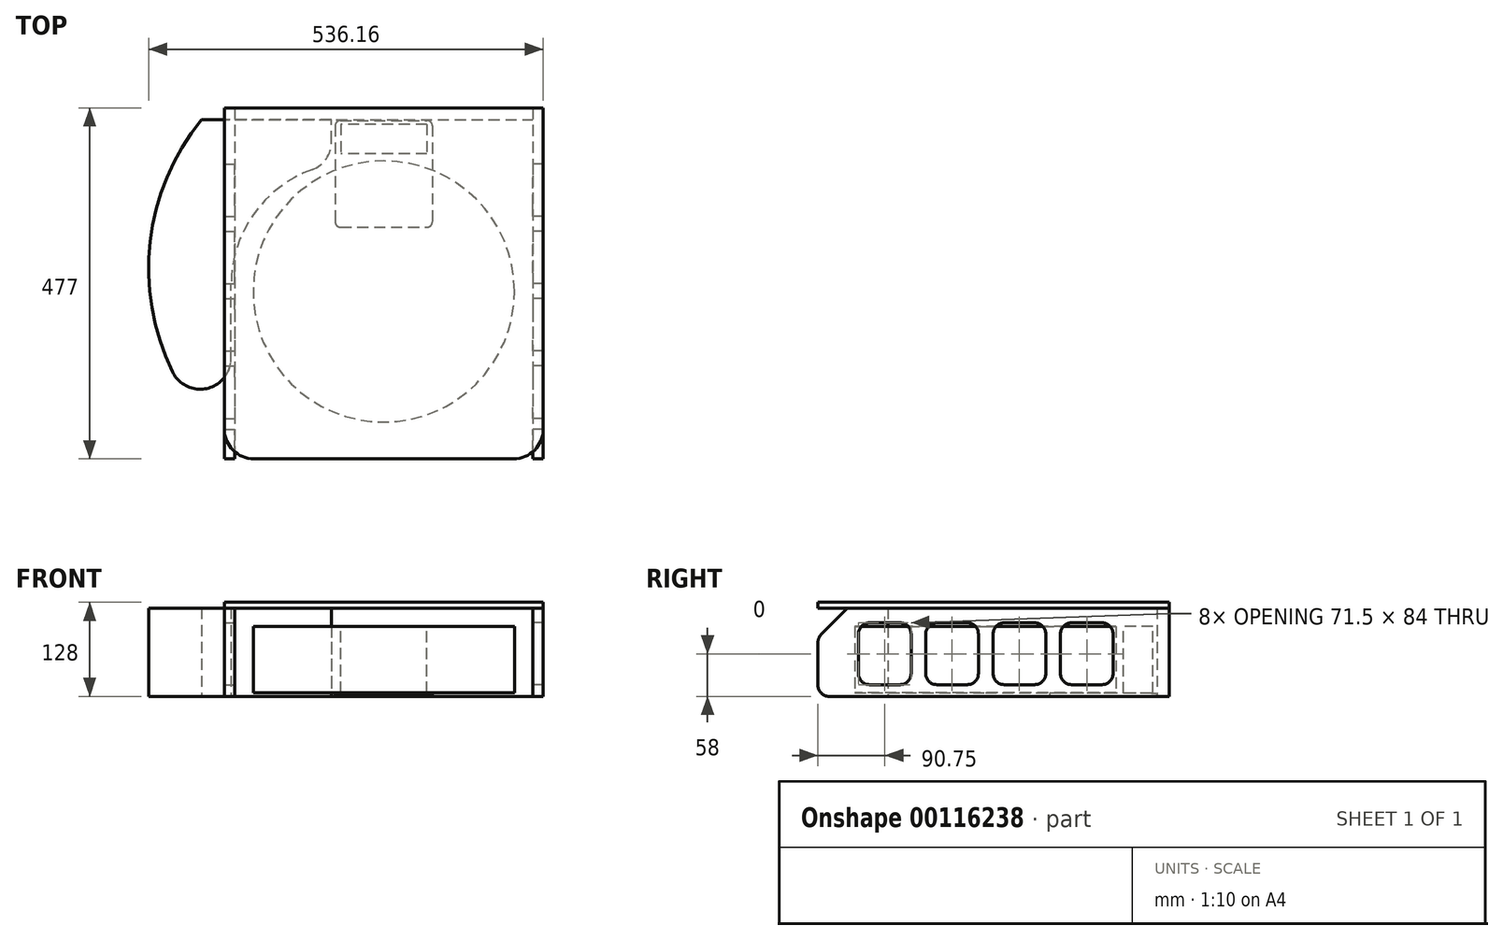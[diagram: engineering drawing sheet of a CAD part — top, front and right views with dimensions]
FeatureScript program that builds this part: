
annotation { "Feature Type Name" : "Feature", "Feature Type Description" : "" }
export const myFeature = defineFeature(function(context is Context, id is Id, definition is map)
    precondition{}
    {
        {
            var Q0;
            Q0=qCreatedBy(makeId("Front.planeOp"),FACE);
            var sketch = newSketch(context, id + "F0", { "sketchPlane" : qUnion([Q0])});
            skLineSegment(sketch, "E0", {"start": v(0, 0) * mm, "end": v(0, 117.94) * mm, "construction": true});
            skPoint(sketch, "E1", {"position": v(0, 5) * mm});
            skPoint(sketch, "E2", {"position": v(0, 95) * mm});
            skSolve(sketch);
        }
        {
            var Q0;
            Q0=qCreatedBy(makeId("Top.planeOp"),FACE);
            var Q1;
            Q1=sQuery(id+"F0.wireOp",VERTEX,"E1");
            cPlane(context, id + "F1", {"entities" : qUnion([Q0, Q1]), "cplaneType" : CPlaneType.PLANE_POINT, "offset" : 25 * mm, "width" : 150 * mm, "height" : 150 * mm});
        }
        {
            var Q0;
            Q0=qCreatedBy(id+"F1.planeOp",FACE);
            var sketch = newSketch(context, id + "F2", { "sketchPlane" : qUnion([Q0])});
            skCircle(sketch, "E3", {"center": v(0, 0) * mm, "radius": 177.5 * mm});
            skSolve(sketch);
        }
        {
            var Q0;
            Q0=qSketchRegion(id+"F2",true);
            extrude(context, id + "F3", {"entities" : qUnion([Q0]), "depth" : 90 * mm});
        }
        {
            var Q0;
            Q0=qCreatedBy(id+"F1.planeOp",FACE);
            var sketch = newSketch(context, id + "F4", { "sketchPlane" : qUnion([Q0])});
            skLineSegment(sketch, "E4.bottom", {"start": v(-58.5, 227.5) * mm, "end": v(58.5, 227.5) * mm});
            skLineSegment(sketch, "E4.top", {"start": v(-58.5, 187.5) * mm, "end": v(58.5, 187.5) * mm});
            skLineSegment(sketch, "E4.left", {"start": v(-58.5, 187.5) * mm, "end": v(-58.5, 227.5) * mm});
            skLineSegment(sketch, "E4.right", {"start": v(58.5, 187.5) * mm, "end": v(58.5, 227.5) * mm});
            skLineSegment(sketch, "E5", {"start": v(0, 0) * mm, "end": v(0, 187.5) * mm, "construction": true});
            skSolve(sketch);
        }
        {
            var Q0;
            Q0=qSketchRegion(id+"F4",true);
            var Q1;
            Q1=qCreatedBy(makeId("Top.planeOp"),FACE);
            var Q2;
            Q2=makeQuery(id+"F3.opExtrude","CAP_FACE",FACE,{"disambiguationData":[OSD([sQuery(id+"F2.wireOp",EDGE,"E3")])],"isStart":false});
            extrude(context, id + "F5", {"entities" : qUnion([Q0]), "endBound" : BoundingType.UP_TO_SURFACE, "oppositeDirection" : true, "endBoundEntityFace" : qUnion([Q1]), "depth" : 100 * mm, "hasSecondDirection" : true, "secondDirectionBound" : SecondDirectionBoundingType.UP_TO_SURFACE, "secondDirectionOppositeDirection" : false, "secondDirectionBoundEntityFace" : qUnion([Q2]), "secondDirectionDepth" : 25 * mm});
        }
        {
            var Q0;
            Q0=qCreatedBy(makeId("Top.planeOp"),FACE);
            var sketch = newSketch(context, id + "F6", { "sketchPlane" : qUnion([Q0])});
            skLineSegment(sketch, "E6.bottom", {"start": v(-59, 232.5) * mm, "end": v(59, 232.5) * mm});
            skLineSegment(sketch, "E6.top", {"start": v(-59, 87.5) * mm, "end": v(59, 87.5) * mm});
            skLineSegment(sketch, "E6.left", {"start": v(-66, 225.5) * mm, "end": v(-66, 94.5) * mm});
            skLineSegment(sketch, "E6.right", {"start": v(66, 225.5) * mm, "end": v(66, 94.5) * mm});
            skPoint(sketch, "E7.visualSharp", {"position": v(-66, 232.5) * mm});
            skArc(sketch, "E7.filletArc", {"start": v(-59, 232.5) * mm, "mid": v(-63.95, 230.45) * mm, "end": v(-66, 225.5) * mm});
            skPoint(sketch, "E8.visualSharp", {"position": v(66, 232.5) * mm});
            skArc(sketch, "E8.filletArc", {"start": v(66, 225.5) * mm, "mid": v(63.95, 230.45) * mm, "end": v(59, 232.5) * mm});
            skPoint(sketch, "E9.visualSharp", {"position": v(66, 87.5) * mm});
            skArc(sketch, "E9.filletArc", {"start": v(59, 87.5) * mm, "mid": v(63.95, 89.55) * mm, "end": v(66, 94.5) * mm});
            skPoint(sketch, "E10.visualSharp", {"position": v(-66, 87.5) * mm});
            skArc(sketch, "E10.filletArc", {"start": v(-66, 94.5) * mm, "mid": v(-63.95, 89.55) * mm, "end": v(-59, 87.5) * mm});
            skLineSegment(sketch, "E11", {"start": v(0, 0) * mm, "end": v(0, 87.5) * mm, "construction": true});
            skSolve(sketch);
        }
        {
            var Q0;
            Q0=qSketchRegion(id+"F6",true);
            extrude(context, id + "F7", {"entities" : qUnion([Q0]), "operationType" : NewBodyOperationType.ADD, "depth" : 4.5 * mm});
        }
        {
            var Q0;
            Q0=makeQuery(id+"F2.imprint","IMPRINT",FACE,{"disambiguationData":[TD([[makeQuery(id+"F2.imprint","IMPRINT",EDGE,{"derivedFrom":sQuery(id+"F2.wireOp",EDGE,"E3")}),1.0]])]});
            var sketch = newSketch(context, id + "F8", { "sketchPlane" : qUnion([Q0])});
            skLineSegment(sketch, "E12", {"start": v(0, -177.5) * mm, "end": v(0, 233.5) * mm, "construction": true});
            skLineSegment(sketch, "E13", {"start": v(-177.5, 233.5) * mm, "end": v(0, 233.5) * mm, "construction": true});
            skLineSegment(sketch, "E14", {"start": v(-177.5, 233.5) * mm, "end": v(-177.5, -177.5) * mm, "construction": true});
            skLineSegment(sketch, "E15", {"start": v(0, -177.5) * mm, "end": v(-177.5, -177.5) * mm, "construction": true});
            skSolve(sketch);
        }
        {
            var Q0;
            Q0=qCreatedBy(makeId("Front.planeOp"),FACE);
            var Q1;
            Q1=sQuery(id+"F8.wireOp",VERTEX,"E12.end");
            cPlane(context, id + "F9", {"entities" : qUnion([Q0, Q1]), "cplaneType" : CPlaneType.PLANE_POINT, "offset" : 25 * mm, "width" : 150 * mm, "height" : 150 * mm});
        }
        {
            var Q0;
            Q0=qCreatedBy(id+"F9.planeOp",FACE);
            var sketch = newSketch(context, id + "F10", { "sketchPlane" : qUnion([Q0])});
            skLineSegment(sketch, "E16.bottom", {"start": v(-202.5, 120) * mm, "end": v(0, 120) * mm});
            skLineSegment(sketch, "E16.top", {"start": v(-202.5, 0) * mm, "end": v(0, 0) * mm});
            skLineSegment(sketch, "E16.left", {"start": v(-202.5, 120) * mm, "end": v(-202.5, 0) * mm});
            skLineSegment(sketch, "E16.right", {"start": v(0, 120) * mm, "end": v(0, 0) * mm});
            skLineSegment(sketch, "E17", {"start": v(-156.5, 114) * mm, "end": v(-200.5, 114) * mm, "construction": true});
            skLineSegment(sketch, "E18", {"start": v(-200.5, 114) * mm, "end": v(-200.5, 76.5) * mm, "construction": true});
            skLineSegment(sketch, "E19", {"start": v(-156.5, 76.5) * mm, "end": v(-156.5, 114) * mm, "construction": true});
            skLineSegment(sketch, "E20", {"start": v(-156.5, 76.5) * mm, "end": v(-200.5, 76.5) * mm, "construction": true});
            skLineSegment(sketch, "E21", {"start": v(-156.5, 90) * mm, "end": v(-162.5, 90) * mm, "construction": true});
            skLineSegment(sketch, "E22", {"start": v(-162.5, 90) * mm, "end": v(-194.5, 90) * mm, "construction": true});
            skLineSegment(sketch, "E23", {"start": v(-194.5, 90) * mm, "end": v(-200.5, 90) * mm, "construction": true});
            skLineSegment(sketch, "E24", {"start": v(-156.5, 108) * mm, "end": v(-162.5, 108) * mm, "construction": true});
            skLineSegment(sketch, "E25", {"start": v(-162.5, 108) * mm, "end": v(-194.5, 108) * mm, "construction": true});
            skLineSegment(sketch, "E26", {"start": v(-194.5, 108) * mm, "end": v(-200.5, 108) * mm, "construction": true});
            skCircle(sketch, "E27", {"center": v(-162.5, 108) * mm, "radius": 2 * mm, "construction": true});
            skCircle(sketch, "E28", {"center": v(-194.5, 108) * mm, "radius": 2 * mm, "construction": true});
            skCircle(sketch, "E29", {"center": v(-194.5, 90) * mm, "radius": 2 * mm, "construction": true});
            skCircle(sketch, "E30", {"center": v(-162.5, 90) * mm, "radius": 2 * mm, "construction": true});
            skLineSegment(sketch, "E31", {"start": v(-162.5, 90) * mm, "end": v(-194.5, 108) * mm, "construction": true});
            skLineSegment(sketch, "E32", {"start": v(-162.5, 108) * mm, "end": v(-194.5, 90) * mm, "construction": true});
            skPoint(sketch, "E33", {"position": v(-178.5, 99) * mm});
            skSolve(sketch);
        }
        {
            var Q0;
            Q0=qSketchRegion(id+"F10",true);
            extrude(context, id + "F11", {"entities" : qUnion([Q0]), "oppositeDirection" : true, "depth" : 16 * mm});
        }
        {
            var Q0;
            Q0=makeQuery(id+"F11.opExtrude","SWEPT_FACE",FACE,{"disambiguationData":[OSD([sQuery(id+"F10.wireOp",EDGE,"E16.top")])]});
            var sketch = newSketch(context, id + "F12", { "sketchPlane" : qUnion([Q0])});
            skLineSegment(sketch, "E34", {"start": v(-247.44, -233.5) * mm, "end": v(-71, -233.5) * mm});
            skLineSegment(sketch, "E35", {"start": v(-71, -233.5) * mm, "end": v(-71, -203.5) * mm});
            skArc(sketch, "E36", {"start": v(-71, -203.5) * mm, "mid": v(-78.23, -180.56) * mm, "end": v(-97.32, -165.91) * mm});
            skArc(sketch, "E37", {"start": v(-207.5, -8.56) * mm, "mid": v(-177.22, -104.6) * mm, "end": v(-97.32, -165.91) * mm});
            skArc(sketch, "E38", {"start": v(-287.2, 109.22) * mm, "mid": v(-317.53, -67.96) * mm, "end": v(-247.44, -233.5) * mm});
            skLineSegment(sketch, "E39", {"start": v(-207.5, -8.56) * mm, "end": v(-207.5, 90.8) * mm});
            skArc(sketch, "E40", {"start": v(-207.5, 90.8) * mm, "mid": v(-240.02, 131.7) * mm, "end": v(-287.2, 109.22) * mm});
            skLineSegment(sketch, "E41", {"start": v(-71, -203.5) * mm, "end": v(-111, -203.5) * mm, "construction": true});
            skLineSegment(sketch, "E42", {"start": v(-111, -203.5) * mm, "end": v(-97.32, -165.91) * mm, "construction": true});
            skSolve(sketch);
        }
        {
            var Q0;
            Q0=qCreatedBy(makeId("Front.planeOp"),FACE);
            var Q1;
            Q1=sQuery(id+"F8.wireOp",VERTEX,"E15.start");
            cPlane(context, id + "F13", {"entities" : qUnion([Q0, Q1]), "cplaneType" : CPlaneType.PLANE_POINT, "offset" : 25 * mm, "width" : 150 * mm, "height" : 150 * mm});
        }
        {
            var Q0;
            Q0=makeQuery(id+"F11.opExtrude","SWEPT_FACE",FACE,{"disambiguationData":[OSD([sQuery(id+"F10.wireOp",EDGE,"E16.left")])]});
            var sketch = newSketch(context, id + "F14", { "sketchPlane" : qUnion([Q0])});
            skLineSegment(sketch, "E43", {"start": v(-249.5, 120) * mm, "end": v(-249.5, 0) * mm});
            skLineSegment(sketch, "E44", {"start": v(227.5, 0) * mm, "end": v(-249.5, 0) * mm});
            skLineSegment(sketch, "E45", {"start": v(227.5, 0) * mm, "end": v(227.5, 80) * mm});
            skLineSegment(sketch, "E46", {"start": v(227.5, 80) * mm, "end": v(187.5, 120) * mm});
            skLineSegment(sketch, "E47", {"start": v(-249.5, 120) * mm, "end": v(187.5, 120) * mm});
            skLineSegment(sketch, "E48.bottom", {"start": v(-102, 100) * mm, "end": v(-173.5, 100) * mm});
            skLineSegment(sketch, "E48.top", {"start": v(-102, 16) * mm, "end": v(-173.5, 16) * mm});
            skLineSegment(sketch, "E48.left", {"start": v(-173.5, 100) * mm, "end": v(-173.5, 16) * mm});
            skLineSegment(sketch, "E48.right", {"start": v(-102, 100) * mm, "end": v(-102, 16) * mm});
            skLineSegment(sketch, "E49.bottom", {"start": v(-10.5, 100) * mm, "end": v(-82, 100) * mm});
            skLineSegment(sketch, "E49.left", {"start": v(-82, 100) * mm, "end": v(-82, 16) * mm});
            skLineSegment(sketch, "E50.top", {"start": v(-10.5, 16) * mm, "end": v(-82, 16) * mm});
            skLineSegment(sketch, "E50.left", {"start": v(-10.5, 100) * mm, "end": v(-10.5, 16) * mm});
            skLineSegment(sketch, "E51.bottom", {"start": v(101, 100) * mm, "end": v(172.5, 100) * mm});
            skLineSegment(sketch, "E51.top", {"start": v(101, 16) * mm, "end": v(172.5, 16) * mm});
            skLineSegment(sketch, "E51.left", {"start": v(101, 100) * mm, "end": v(101, 16) * mm});
            skLineSegment(sketch, "E51.right", {"start": v(172.5, 100) * mm, "end": v(172.5, 16) * mm});
            skLineSegment(sketch, "E52", {"start": v(227.5, 80) * mm, "end": v(227.5, 120) * mm, "construction": true});
            skLineSegment(sketch, "E53.bottom", {"start": v(9.5, 100) * mm, "end": v(81, 100) * mm});
            skLineSegment(sketch, "E53.top", {"start": v(9.5, 16) * mm, "end": v(81, 16) * mm});
            skLineSegment(sketch, "E53.left", {"start": v(81, 100) * mm, "end": v(81, 16) * mm});
            skLineSegment(sketch, "E53.right", {"start": v(9.5, 100) * mm, "end": v(9.5, 16) * mm});
            skPoint(sketch, "E54", {"position": v(101, 120) * mm});
            skLineSegment(sketch, "E55", {"start": v(187.5, 120) * mm, "end": v(187.5, 0) * mm, "construction": true});
            skLineSegment(sketch, "E56", {"start": v(-102, 16) * mm, "end": v(-82, 16) * mm, "construction": true});
            skLineSegment(sketch, "E57", {"start": v(9.5, 16) * mm, "end": v(-10.5, 16) * mm, "construction": true});
            skLineSegment(sketch, "E58", {"start": v(81, 16) * mm, "end": v(101, 16) * mm, "construction": true});
            skPoint(sketch, "E59", {"position": v(177.5, 23.11) * mm});
            skSolve(sketch);
        }
        {
            var Q0;
            Q0=qSketchRegion(id+"F14",true);
            extrude(context, id + "F15", {"entities" : qUnion([Q0]), "depth" : 14 * mm});
        }
        {
            var Q0;
            Q0=makeQuery(id+"F15.opExtrude","SWEPT_FACE",FACE,{"disambiguationData":[OSD([sQuery(id+"F14.wireOp",EDGE,"E47")])]});
            var sketch = newSketch(context, id + "F16", { "sketchPlane" : qUnion([Q0])});
            skLineSegment(sketch, "E60", {"start": v(-216.5, -144.25) * mm, "end": v(-202.5, -144.25) * mm, "construction": true});
            skCircle(sketch, "E61", {"center": v(-209.5, -144.25) * mm, "radius": 5.05 * mm});
            skSolve(sketch);
        }
        {
            var Q0;
            Q0=makeQuery(id+"F15.opExtrude","SWEPT_EDGE",EDGE,{"disambiguationData":[OSD([sQuery(id+"F14.wireOp",EDGE,"E49.bottom"),sQuery(id+"F14.wireOp",EDGE,"E49.left")])]});
            var Q1;
            Q1=makeQuery(id+"F15.opExtrude","SWEPT_EDGE",EDGE,{"disambiguationData":[OSD([sQuery(id+"F14.wireOp",EDGE,"E48.bottom"),sQuery(id+"F14.wireOp",EDGE,"E48.left")])]});
            var Q2;
            Q2=makeQuery(id+"F15.opExtrude","SWEPT_EDGE",EDGE,{"disambiguationData":[OSD([sQuery(id+"F14.wireOp",EDGE,"E50.bottom"),sQuery(id+"F14.wireOp",EDGE,"E50.left")])]});
            var Q3;
            Q3=makeQuery(id+"F15.opExtrude","SWEPT_EDGE",EDGE,{"disambiguationData":[OSD([sQuery(id+"F14.wireOp",EDGE,"E44"),sQuery(id+"F14.wireOp",EDGE,"E45")])]});
            var Q4;
            Q4=makeQuery(id+"F15.opExtrude","SWEPT_EDGE",EDGE,{"disambiguationData":[OSD([sQuery(id+"F14.wireOp",EDGE,"E45"),sQuery(id+"F14.wireOp",EDGE,"E46")])]});
            var Q5;
            Q5=makeQuery(id+"F15.opExtrude","SWEPT_EDGE",EDGE,{"disambiguationData":[OSD([sQuery(id+"F14.wireOp",EDGE,"E48.top"),sQuery(id+"F14.wireOp",EDGE,"E48.left")])]});
            var Q6;
            Q6=makeQuery(id+"F15.opExtrude","SWEPT_EDGE",EDGE,{"disambiguationData":[OSD([sQuery(id+"F14.wireOp",EDGE,"E49.top"),sQuery(id+"F14.wireOp",EDGE,"E49.left")])]});
            var Q7;
            Q7=makeQuery(id+"F15.opExtrude","SWEPT_EDGE",EDGE,{"disambiguationData":[OSD([sQuery(id+"F14.wireOp",EDGE,"E50.top"),sQuery(id+"F14.wireOp",EDGE,"E50.left")])]});
            var Q8;
            Q8=makeQuery(id+"F15.opExtrude","SWEPT_EDGE",EDGE,{"disambiguationData":[OSD([sQuery(id+"F14.wireOp",EDGE,"E50.top"),sQuery(id+"F14.wireOp",EDGE,"E50.right")])]});
            var Q9;
            Q9=makeQuery(id+"F15.opExtrude","SWEPT_EDGE",EDGE,{"disambiguationData":[OSD([sQuery(id+"F14.wireOp",EDGE,"E49.top"),sQuery(id+"F14.wireOp",EDGE,"E49.right")])]});
            var Q10;
            Q10=makeQuery(id+"F15.opExtrude","SWEPT_EDGE",EDGE,{"disambiguationData":[OSD([sQuery(id+"F14.wireOp",EDGE,"E48.top"),sQuery(id+"F14.wireOp",EDGE,"E48.right")])]});
            var Q11;
            Q11=makeQuery(id+"F15.opExtrude","SWEPT_EDGE",EDGE,{"disambiguationData":[OSD([sQuery(id+"F14.wireOp",EDGE,"E50.bottom"),sQuery(id+"F14.wireOp",EDGE,"E50.right")])]});
            var Q12;
            Q12=makeQuery(id+"F15.opExtrude","SWEPT_EDGE",EDGE,{"disambiguationData":[OSD([sQuery(id+"F14.wireOp",EDGE,"E49.bottom"),sQuery(id+"F14.wireOp",EDGE,"E49.right")])]});
            var Q13;
            Q13=makeQuery(id+"F15.opExtrude","SWEPT_EDGE",EDGE,{"disambiguationData":[OSD([sQuery(id+"F14.wireOp",EDGE,"E48.bottom"),sQuery(id+"F14.wireOp",EDGE,"E48.right")])]});
            var Q14;
            Q14=makeQuery(id+"F15.opExtrude","SWEPT_EDGE",EDGE,{"disambiguationData":[OSD([sQuery(id+"F14.wireOp",EDGE,"E51.top"),sQuery(id+"F14.wireOp",EDGE,"E51.left")])]});
            var Q15;
            Q15=makeQuery(id+"F15.opExtrude","SWEPT_EDGE",EDGE,{"disambiguationData":[OSD([sQuery(id+"F14.wireOp",EDGE,"E51.top"),sQuery(id+"F14.wireOp",EDGE,"E51.right")])]});
            var Q16;
            Q16=makeQuery(id+"F15.opExtrude","SWEPT_EDGE",EDGE,{"disambiguationData":[OSD([sQuery(id+"F14.wireOp",EDGE,"E51.bottom"),sQuery(id+"F14.wireOp",EDGE,"E51.right")])]});
            var Q17;
            Q17=makeQuery(id+"F15.opExtrude","SWEPT_EDGE",EDGE,{"disambiguationData":[OSD([sQuery(id+"F14.wireOp",EDGE,"E51.bottom"),sQuery(id+"F14.wireOp",EDGE,"E51.left")])]});
            var Q18;
            Q18=makeQuery(id+"F11.opExtrude","SWEPT_EDGE",EDGE,{"disambiguationData":[OSD([sQuery(id+"F10.wireOp",EDGE,"42908f74-1b4f-4dd7-a1f5-b5feeaa3a12f.bottom"),sQuery(id+"F10.wireOp",EDGE,"42908f74-1b4f-4dd7-a1f5-b5feeaa3a12f.right")])]});
            var Q19;
            Q19=makeQuery(id+"F11.opExtrude","SWEPT_EDGE",EDGE,{"disambiguationData":[OSD([sQuery(id+"F10.wireOp",EDGE,"7d3d7e17-e7ec-4853-b92f-0c4755d0859e.bottom"),sQuery(id+"F10.wireOp",EDGE,"7d3d7e17-e7ec-4853-b92f-0c4755d0859e.right")])]});
            var Q20;
            Q20=makeQuery(id+"F11.opExtrude","SWEPT_EDGE",EDGE,{"disambiguationData":[OSD([sQuery(id+"F10.wireOp",EDGE,"7d3d7e17-e7ec-4853-b92f-0c4755d0859e.top"),sQuery(id+"F10.wireOp",EDGE,"7d3d7e17-e7ec-4853-b92f-0c4755d0859e.right")])]});
            var Q21;
            Q21=makeQuery(id+"F11.opExtrude","SWEPT_EDGE",EDGE,{"disambiguationData":[OSD([sQuery(id+"F10.wireOp",EDGE,"42908f74-1b4f-4dd7-a1f5-b5feeaa3a12f.top"),sQuery(id+"F10.wireOp",EDGE,"42908f74-1b4f-4dd7-a1f5-b5feeaa3a12f.right")])]});
            var Q22;
            Q22=makeQuery(id+"F11.opExtrude","SWEPT_EDGE",EDGE,{"disambiguationData":[OSD([sQuery(id+"F10.wireOp",EDGE,"7d3d7e17-e7ec-4853-b92f-0c4755d0859e.bottom"),sQuery(id+"F10.wireOp",EDGE,"7d3d7e17-e7ec-4853-b92f-0c4755d0859e.left")])]});
            var Q23;
            Q23=makeQuery(id+"F11.opExtrude","SWEPT_EDGE",EDGE,{"disambiguationData":[OSD([sQuery(id+"F10.wireOp",EDGE,"42908f74-1b4f-4dd7-a1f5-b5feeaa3a12f.bottom"),sQuery(id+"F10.wireOp",EDGE,"42908f74-1b4f-4dd7-a1f5-b5feeaa3a12f.left")])]});
            var Q24;
            Q24=makeQuery(id+"F11.opExtrude","SWEPT_EDGE",EDGE,{"disambiguationData":[OSD([sQuery(id+"F10.wireOp",EDGE,"42908f74-1b4f-4dd7-a1f5-b5feeaa3a12f.top"),sQuery(id+"F10.wireOp",EDGE,"42908f74-1b4f-4dd7-a1f5-b5feeaa3a12f.left")])]});
            var Q25;
            Q25=makeQuery(id+"F11.opExtrude","SWEPT_EDGE",EDGE,{"disambiguationData":[OSD([sQuery(id+"F10.wireOp",EDGE,"7d3d7e17-e7ec-4853-b92f-0c4755d0859e.top"),sQuery(id+"F10.wireOp",EDGE,"7d3d7e17-e7ec-4853-b92f-0c4755d0859e.left")])]});
            var Q26;
            Q26=makeQuery(id+"F15.opExtrude","SWEPT_EDGE",EDGE,{"disambiguationData":[OSD([sQuery(id+"F14.wireOp",EDGE,"E53.top"),sQuery(id+"F14.wireOp",EDGE,"E53.right")])]});
            var Q27;
            Q27=makeQuery(id+"F15.opExtrude","SWEPT_EDGE",EDGE,{"disambiguationData":[OSD([sQuery(id+"F14.wireOp",EDGE,"E53.bottom"),sQuery(id+"F14.wireOp",EDGE,"E53.right")])]});
            var Q28;
            Q28=makeQuery(id+"F15.opExtrude","SWEPT_EDGE",EDGE,{"disambiguationData":[OSD([sQuery(id+"F14.wireOp",EDGE,"E53.top"),sQuery(id+"F14.wireOp",EDGE,"E53.left")])]});
            var Q29;
            Q29=makeQuery(id+"F15.opExtrude","SWEPT_EDGE",EDGE,{"disambiguationData":[OSD([sQuery(id+"F14.wireOp",EDGE,"E53.bottom"),sQuery(id+"F14.wireOp",EDGE,"E53.left")])]});
            fillet(context, id + "F17", {"entities" : qUnion([Q0, Q1, Q2, Q3, Q4, Q5, Q6, Q7, Q8, Q9, Q10, Q11, Q12, Q13, Q14, Q15, Q16, Q17, Q18, Q19, Q20, Q21, Q22, Q23, Q24, Q25, Q26, Q27, Q28, Q29]), "radius" : 15 * mm, "tangentPropagation" : true, "allowEdgeOverflow" : false});
        }
        {
            var Q0;
            Q0=makeQuery(id+"F11.opExtrude","SWEPT_BODY",BODY,{"disambiguationData":[OSD([sQuery(id+"F10.wireOp",EDGE,"E16.bottom"),sQuery(id+"F10.wireOp",EDGE,"E16.top"),sQuery(id+"F10.wireOp",EDGE,"E16.left"),sQuery(id+"F10.wireOp",EDGE,"E16.right"),sQuery(id+"F10.wireOp",EDGE,"5cda8c20-23ce-490b-b1d3-2776b074a77f"),sQuery(id+"F10.wireOp",EDGE,"887f5a22-7d88-485e-85bc-e6de6f7dc943"),sQuery(id+"F10.wireOp",EDGE,"7d3d7e17-e7ec-4853-b92f-0c4755d0859e.bottom"),sQuery(id+"F10.wireOp",EDGE,"7d3d7e17-e7ec-4853-b92f-0c4755d0859e.top"),sQuery(id+"F10.wireOp",EDGE,"7d3d7e17-e7ec-4853-b92f-0c4755d0859e.left"),sQuery(id+"F10.wireOp",EDGE,"7d3d7e17-e7ec-4853-b92f-0c4755d0859e.right")])]});
            var Q1;
            Q1=qCreatedBy(makeId("Right.planeOp"),FACE);
            mirror(context, id + "F18", {"entities" : qUnion([Q0]), "mirrorPlane" : qUnion([Q1])});
        }
        {
            var Q0;
            Q0=makeQuery(id+"F15.opExtrude","SWEPT_BODY",BODY,{"disambiguationData":[OSD([sQuery(id+"F14.wireOp",EDGE,"E43"),sQuery(id+"F14.wireOp",EDGE,"E44"),sQuery(id+"F14.wireOp",EDGE,"E45"),sQuery(id+"F14.wireOp",EDGE,"E46"),sQuery(id+"F14.wireOp",EDGE,"E47"),sQuery(id+"F14.wireOp",EDGE,"E48.bottom"),sQuery(id+"F14.wireOp",EDGE,"E48.top"),sQuery(id+"F14.wireOp",EDGE,"E48.left"),sQuery(id+"F14.wireOp",EDGE,"E48.right"),sQuery(id+"F14.wireOp",EDGE,"E49.bottom"),sQuery(id+"F14.wireOp",EDGE,"E49.left"),sQuery(id+"F14.wireOp",EDGE,"E50.top"),sQuery(id+"F14.wireOp",EDGE,"E50.left"),sQuery(id+"F14.wireOp",EDGE,"E51.bottom"),sQuery(id+"F14.wireOp",EDGE,"E51.top"),sQuery(id+"F14.wireOp",EDGE,"E51.left"),sQuery(id+"F14.wireOp",EDGE,"E51.right")])]});
            var Q1;
            Q1=qCreatedBy(makeId("Right.planeOp"),FACE);
            mirror(context, id + "F19", {"entities" : qUnion([Q0]), "mirrorPlane" : qUnion([Q1])});
        }
        {
            var Q0;
            Q0=qCreatedBy(makeId("Top.planeOp"),FACE);
            var Q1;
            Q1=makeQuery(id+"F18.opPattern","COPY",VERTEX,{"derivedFrom":makeQuery(id+"F11.opExtrude","CAP_VERTEX",VERTEX,{"disambiguationData":[OSD([sQuery(id+"F10.wireOp",EDGE,"E16.bottom"),sQuery(id+"F10.wireOp",EDGE,"E16.right")])],"isStart":true}),"instanceName":"1"});
            cPlane(context, id + "F20", {"entities" : qUnion([Q0, Q1]), "cplaneType" : CPlaneType.PLANE_POINT, "offset" : 150 * mm, "width" : 150 * mm, "height" : 150 * mm});
        }
        {
            var Q0;
            Q0=qCreatedBy(id+"F20.planeOp",FACE);
            var sketch = newSketch(context, id + "F21", { "sketchPlane" : qUnion([Q0])});
            skLineSegment(sketch, "E62.bottom", {"start": v(216.5, 249.5) * mm, "end": v(-216.5, 249.5) * mm});
            skLineSegment(sketch, "E62.top", {"start": v(176.5, -227.5) * mm, "end": v(-176.5, -227.5) * mm});
            skLineSegment(sketch, "E62.left", {"start": v(-216.5, 249.5) * mm, "end": v(-216.5, -187.5) * mm});
            skLineSegment(sketch, "E62.right", {"start": v(216.5, 249.5) * mm, "end": v(216.5, -187.5) * mm});
            skCircle(sketch, "E63", {"center": v(0, 0) * mm, "radius": 187.5 * mm, "construction": true});
            skLineSegment(sketch, "E64", {"start": v(-216.5, -187.5) * mm, "end": v(216.5, -187.5) * mm, "construction": true});
            skArc(sketch, "E65", {"start": v(-216.5, -187.5) * mm, "mid": v(-204.78, -215.78) * mm, "end": v(-176.5, -227.5) * mm});
            skArc(sketch, "E66", {"start": v(176.5, -227.5) * mm, "mid": v(204.78, -215.78) * mm, "end": v(216.5, -187.5) * mm});
            skSolve(sketch);
        }
        {
            var Q0;
            Q0=qSketchRegion(id+"F21",true);
            extrude(context, id + "F22", {"entities" : qUnion([Q0]), "depth" : 8 * mm});
        }
        {
            var Q0;
            Q0=makeQuery(id+"F11.opExtrude","SWEPT_BODY",BODY,{"disambiguationData":[OSD([sQuery(id+"F10.wireOp",EDGE,"E16.bottom"),sQuery(id+"F10.wireOp",EDGE,"E16.top"),sQuery(id+"F10.wireOp",EDGE,"E16.left"),sQuery(id+"F10.wireOp",EDGE,"E16.right"),sQuery(id+"F10.wireOp",EDGE,"5cda8c20-23ce-490b-b1d3-2776b074a77f"),sQuery(id+"F10.wireOp",EDGE,"887f5a22-7d88-485e-85bc-e6de6f7dc943"),sQuery(id+"F10.wireOp",EDGE,"7d3d7e17-e7ec-4853-b92f-0c4755d0859e.bottom"),sQuery(id+"F10.wireOp",EDGE,"7d3d7e17-e7ec-4853-b92f-0c4755d0859e.top"),sQuery(id+"F10.wireOp",EDGE,"7d3d7e17-e7ec-4853-b92f-0c4755d0859e.left"),sQuery(id+"F10.wireOp",EDGE,"7d3d7e17-e7ec-4853-b92f-0c4755d0859e.right")])]});
            var Q1;
            Q1=makeQuery(id+"F18.opPattern","COPY",BODY,{"derivedFrom":makeQuery(id+"F11.opExtrude","SWEPT_BODY",BODY,{"disambiguationData":[OSD([sQuery(id+"F10.wireOp",EDGE,"E16.bottom"),sQuery(id+"F10.wireOp",EDGE,"E16.top"),sQuery(id+"F10.wireOp",EDGE,"E16.left"),sQuery(id+"F10.wireOp",EDGE,"E16.right"),sQuery(id+"F10.wireOp",EDGE,"5cda8c20-23ce-490b-b1d3-2776b074a77f"),sQuery(id+"F10.wireOp",EDGE,"887f5a22-7d88-485e-85bc-e6de6f7dc943"),sQuery(id+"F10.wireOp",EDGE,"7d3d7e17-e7ec-4853-b92f-0c4755d0859e.bottom"),sQuery(id+"F10.wireOp",EDGE,"7d3d7e17-e7ec-4853-b92f-0c4755d0859e.top"),sQuery(id+"F10.wireOp",EDGE,"7d3d7e17-e7ec-4853-b92f-0c4755d0859e.left"),sQuery(id+"F10.wireOp",EDGE,"7d3d7e17-e7ec-4853-b92f-0c4755d0859e.right")])]}),"instanceName":"1"});
            booleanBodies(context, id + "F23", {"operationType" : BooleanOperationType.UNION, "tools" : qUnion([Q0, Q1])});
        }
        {
            var Q0;
            {var subQ0=sQuery(id+"F12.wireOp",EDGE,"E35");Q0=makeQuery(id+"F12.imprint","IMPRINT",FACE,{"disambiguationData":[TD([[makeQuery(id+"F12.imprint","IMPRINT",EDGE,{"derivedFrom":subQ0}),1.0]])]});}
            var Q1;
            {var subQ0=makeQuery(id+"F11.opExtrude","SWEPT_FACE",FACE,{"disambiguationData":[OSD([sQuery(id+"F10.wireOp",EDGE,"E16.bottom")])]});Q1=makeQuery(id+"F23.opBoolean","MERGE",FACE,{"derivedFrom":[subQ0,makeQuery(id+"F18.opPattern","COPY",FACE,{"derivedFrom":subQ0,"instanceName":"1"})]});}
            extrude(context, id + "F24", {"entities" : qUnion([Q0]), "endBound" : BoundingType.UP_TO_SURFACE, "oppositeDirection" : true, "endBoundEntityFace" : qUnion([Q1]), "depth" : 25 * mm});
        }
    });
